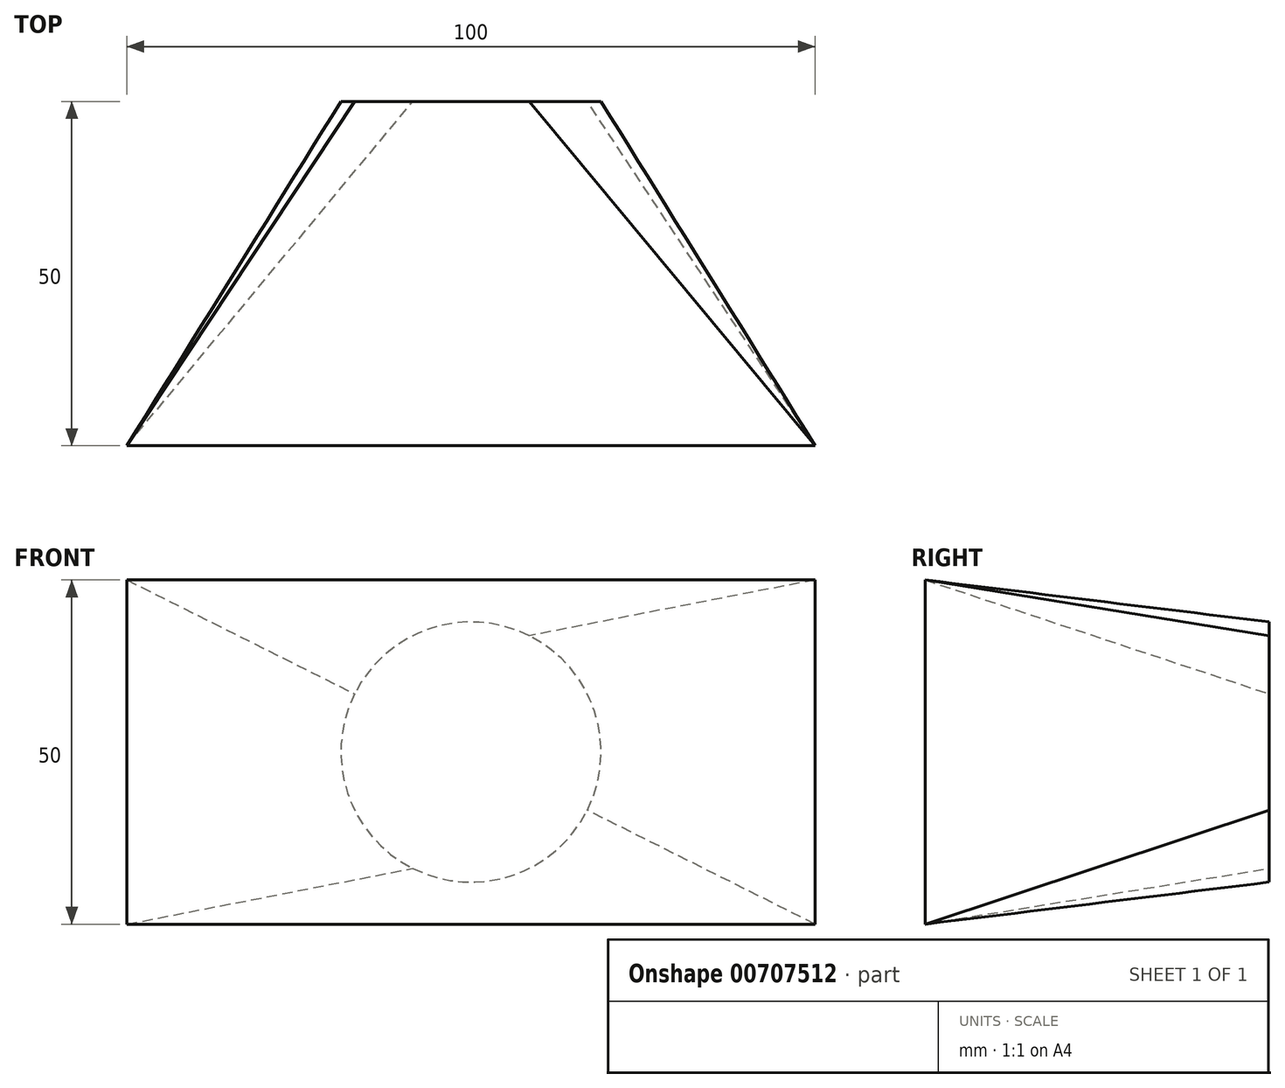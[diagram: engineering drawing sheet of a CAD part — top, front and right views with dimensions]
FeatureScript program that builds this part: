
annotation { "Feature Type Name" : "Feature", "Feature Type Description" : "" }
export const myFeature = defineFeature(function(context is Context, id is Id, definition is map)
    precondition{}
    {
        {
            var Q0;
            Q0=qCreatedBy(makeId("Front.planeOp"),FACE);
            var sketch = newSketch(context, id + "F0", { "sketchPlane" : qUnion([Q0])});
            skLineSegment(sketch, "E0.bottom", {"start": v(-50, 25) * mm, "end": v(50, 25) * mm});
            skLineSegment(sketch, "E0.top", {"start": v(-50, -25) * mm, "end": v(50, -25) * mm});
            skLineSegment(sketch, "E0.left", {"start": v(-50, 25) * mm, "end": v(-50, -25) * mm});
            skLineSegment(sketch, "E0.right", {"start": v(50, 25) * mm, "end": v(50, -25) * mm});
            skSolve(sketch);
        }
        {
            var Q0;
            Q0=qCreatedBy(makeId("Front.planeOp"),FACE);
            cPlane(context, id + "F1", {"entities" : qUnion([Q0]), "cplaneType" : CPlaneType.OFFSET, "offset" : 50 * mm, "oppositeDirection" : true, "width" : 150 * mm, "height" : 150 * mm});
        }
        {
            var Q0;
            Q0=qCreatedBy(id+"F1.planeOp",FACE);
            var sketch = newSketch(context, id + "F2", { "sketchPlane" : qUnion([Q0])});
            skCircle(sketch, "E1", {"center": v(0, 0) * mm, "radius": 18.9 * mm});
            skSolve(sketch);
        }
        {
            var Q0;
            Q0=makeQuery(id+"F0.imprint","IMPRINT",FACE,{"disambiguationData":[TD([[makeQuery(id+"F0.imprint","IMPRINT",EDGE,{"derivedFrom":sQuery(id+"F0.wireOp",EDGE,"E0.bottom")}),-1.0]])]});
            var Q1;
            Q1=makeQuery(id+"F2.imprint","IMPRINT",FACE,{"disambiguationData":[TD([[makeQuery(id+"F2.imprint","IMPRINT",EDGE,{"derivedFrom":sQuery(id+"F2.wireOp",EDGE,"E1")}),1.0]])]});
            loft(context, id + "F3", {"sheetProfilesArray" : [{ "sheetProfileEntities" : qUnion([Q0]) }, { "sheetProfileEntities" : qUnion([Q1]) }]});
        }
    });
